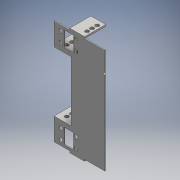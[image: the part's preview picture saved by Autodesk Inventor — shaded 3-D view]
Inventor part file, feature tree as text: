
AUTODESK INVENTOR PART (.ipt)
format: ipt  version: 2016 (Build 200138000, 138)  size: 233,984 bytes
history: native  units: mm
features: sketch x8, hole x4, extrude x3
ambient origin geometry x8: Origin, YZ Plane, XZ Plane, XY Plane, X Axis, Y Axis, Z Axis, Center Point
bodies: Solid1 (feature_tree)
feature tree (15):
  extrude  "Extrusion1"  Depth=24.0mm
  extrude  "Extrusion2"  Depth=76.0mm
  extrude  "Extrusion3"  Depth=24.0mm
  hole  "Hole1"  [1 undecoded]
  hole  "Hole2"  [1 undecoded]
  hole  "Hole3"  [1 undecoded]
  hole  "Hole4"  [1 undecoded]
  sketch  "Sketch13"  dims[d15=3.0mm d16=3.75mm d17=4.4mm d18=3.25mm d19=4.4mm d20=6.0mm d21=8.0mm d22=8.0mm d23=1.5mm d24=0.0mm d29=2.5mm d30=2.5mm d32=18.5mm d33=2.0mm d34=17.5mm d35=24.0mm d36=0.0mm d37=1.0mm d38=0.0mm d39=4.4mm d40=4.0mm d41=6.0mm d42=4.4mm d43=4.4mm d44=6.0mm d45=6.0mm d46=6.0mm d47=4.4mm d48=6.0mm d49=4.0mm d50=2.0mm d51=90.0deg d52=2.0mm d53=0.0mm d54=4.4mm d55=4.4mm d56=4.4mm d57=4.4mm d58=6.0mm d59=4.0mm d60=2.0mm d61=90.0deg d62=2.0mm d63=0.0mm d68=4.4mm d69=8.0mm d70=6.0mm d71=4.4mm d72=4.4mm d73=6.0mm d74=6.0mm d75=4.4mm d76=6.0mm d77=4.0mm d78=2.0mm d79=90.0deg d80=2.5mm d81=0.0mm d82=4.4mm d83=23.5mm d84=4.4mm d85=4.4mm d86=4.4mm d87=4.4mm d88=4.4mm d93=4.4mm d94=6.0mm d95=4.0mm d96=2.0mm d97=90.0deg d98=2.5mm d99=0.0mm]
  sketch  "Sketch1"  dims[d0=60.0mm d1=24.0mm]
  sketch  "Sketch2"  dims[d2=20.0mm d3=76.0mm]
  sketch  "Sketch4"  dims[d4=20.0mm d5=24.0mm]
  sketch  "Sketch6"  dims[d6=1.0mm d7=0.0mm d8=4.4mm]
  sketch  "Sketch7"  dims[d9=6.0mm d10=8.0mm]
  sketch  "Sketch11"  dims[d11=4.4mm d12=12.0mm]
  sketch  "Sketch12"  dims[d13=11.0mm d14=18.0mm]
note: 4 required parameter values undecoded (feature->parameter linkage not recoverable at this tier; creation-order binding heuristic only, values carry confidence <= 0.55)
